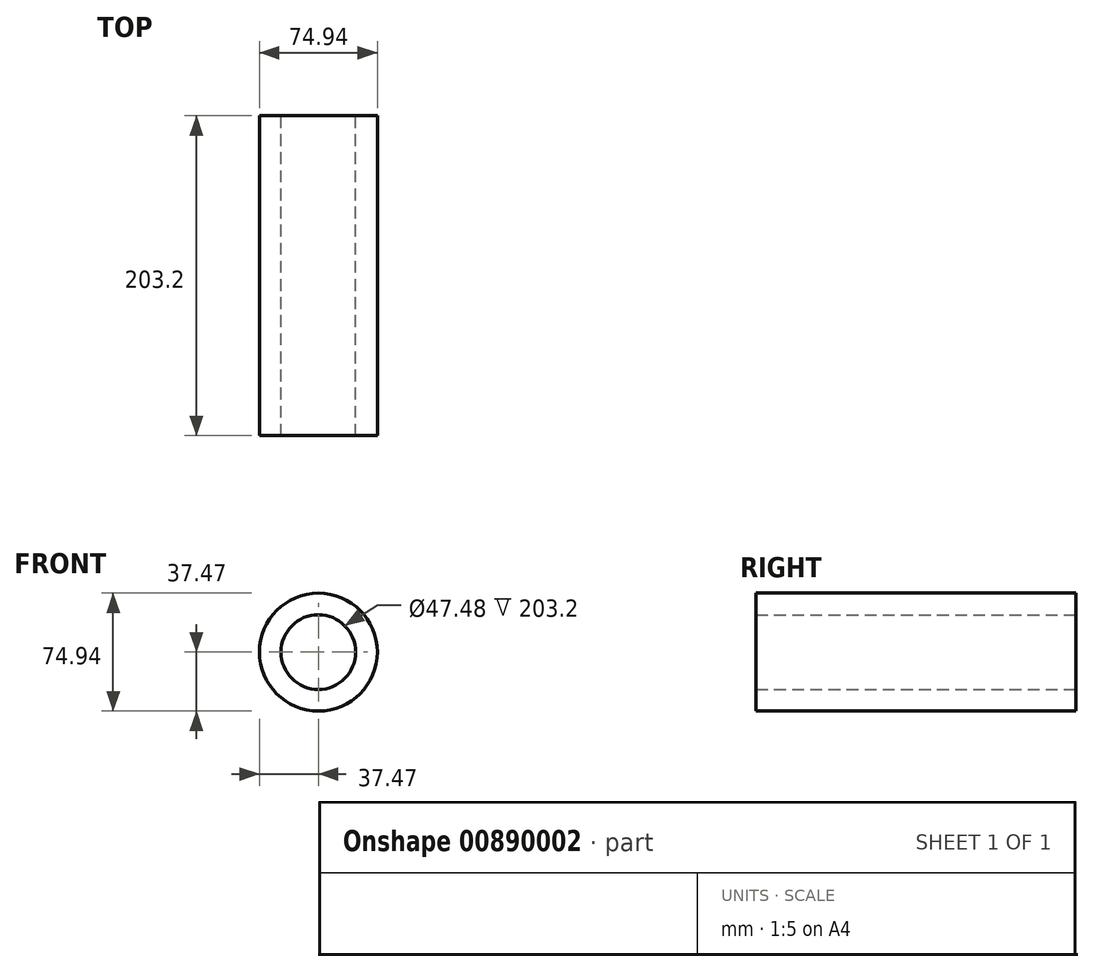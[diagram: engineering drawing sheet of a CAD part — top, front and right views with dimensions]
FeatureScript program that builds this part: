
annotation { "Feature Type Name" : "Feature", "Feature Type Description" : "" }
export const myFeature = defineFeature(function(context is Context, id is Id, definition is map)
    precondition{}
    {
        {
            var Q0;
            Q0=qCreatedBy(makeId("Front.planeOp"),FACE);
            var sketch = newSketch(context, id + "F0", { "sketchPlane" : qUnion([Q0])});
            skCircle(sketch, "E0", {"center": v(0, 0) * mm, "radius": 37.47 * mm});
            skCircle(sketch, "E1", {"center": v(0, 0) * mm, "radius": 23.74 * mm});
            skSolve(sketch);
        }
        {
            var Q0;
            Q0=makeQuery(id+"F0.imprint","IMPRINT",FACE,{"disambiguationData":[TD([[makeQuery(id+"F0.imprint","IMPRINT",EDGE,{"derivedFrom":sQuery(id+"F0.wireOp",EDGE,"E0")}),1.0]])]});
            extrude(context, id + "F1", {"entities" : qUnion([Q0]), "depth" : 203.2 * mm, "offsetDistance" : 25.4 * mm});
        }
    });
